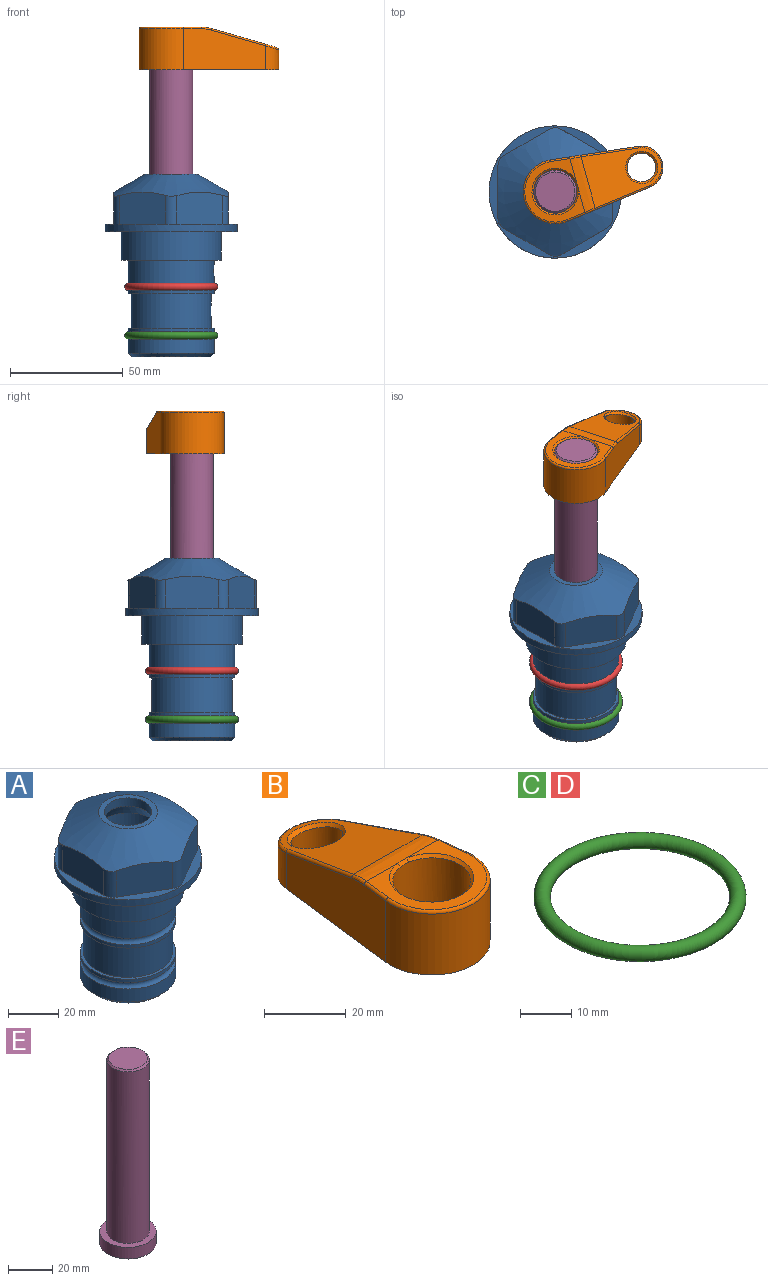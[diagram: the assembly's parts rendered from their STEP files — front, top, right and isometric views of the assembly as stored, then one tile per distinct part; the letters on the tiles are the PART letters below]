
ASSEMBLY  parts=5 mates=4
PART A: 36 faces, bbox 58.7x58.7x81 mm
  f0: cylinder r=17.78mm len=35.56mm, axis (0,0,1), area 1670.8mm2, adj f23,f24,f31
  f1: cylinder r=19.05mm len=38.1mm, axis (0,0,1), area 1191.9mm2, adj f26,f27,f30
  f2: plane 58.66x58.66mm, normal (0,0,-1), area 1150.6mm2, adj f3,f28
  f3: cylinder r=29.33mm len=58.66mm, axis (0,0,-1), area 585.1mm2, adj f2,f4
  f4: plane 58.66x58.66mm, normal (0,0,1), area 475.9mm2, adj f3,f5,f6,f7,f8,f9,f10,f11
  f5: plane 20.32x14.34mm, normal (-0.5,0.87,0), area 324.4mm2, adj f4,f15,f16,f17
  f6: plane 20.32x14.34mm, normal (0.5,0.87,0), area 324.4mm2, adj f4,f14,f15,f17
  f7: plane 23.48x14.34mm, normal (1,0,0), area 324.4mm2, adj f4,f13,f14,f17
  f8: plane 20.32x14.34mm, normal (0.5,-0.87,0), area 324.4mm2, adj f4,f12,f13,f17
  f9: plane 20.32x14.34mm, normal (-0.5,-0.87,0), area 324.4mm2, adj f4,f11,f12,f17
  f10: plane 23.48x14.34mm, normal (-1,0,0), area 324.4mm2, adj f4,f11,f16,f17
  f11: cylinder r=5.08mm len=12.85mm, axis (0,0,-1), area 67.2mm2, adj f4,f9,f10,f17
  f12: cylinder r=5.08mm len=12.85mm, axis (0,0,-1), area 67.2mm2, adj f4,f8,f9,f17
  f13: cylinder r=5.08mm len=12.85mm, axis (0,0,-1), area 67.2mm2, adj f4,f7,f8,f17
  f14: cylinder r=5.08mm len=12.85mm, axis (0,0,-1), area 67.2mm2, adj f4,f6,f7,f17
  f15: cylinder r=5.08mm len=12.85mm, axis (0,0,-1), area 67.2mm2, adj f4,f5,f6,f17
  f16: cylinder r=5.08mm len=12.85mm, axis (0,0,-1), area 67.2mm2, adj f4,f5,f10,f17
  f17: cone r=11.73mm half-angle=60deg, axis (0,0,-1), area 2071.8mm2, adj f5,f6,f7,f8,f9,f10,f11,f12
  f18: plane 23.46x23.46mm, normal (0,0,1), area 147.4mm2, adj f17,f35
  f19: plane 34.93x34.93mm, normal (0,0,-1), area 958mm2, adj f29
  f20: cylinder r=19.05mm len=38.1mm, axis (0,0,1), area 760.1mm2, adj f21,f29
  f21: torus R=19.05mm, axis (0,0,1), area 565.3mm2, adj f20,f22
  f22: cylinder r=19.05mm len=38.1mm, axis (0,0,1), area 190mm2, adj f21,f23
  f23: plane 38.1x38.1mm, normal (0,0,1), area 146.9mm2, adj f0,f22
  f24: plane 38.1x38.1mm, normal (0,0,-1), area 146.9mm2, adj f0,f25
  f25: cylinder r=19.05mm len=38.1mm, axis (0,0,1), area 190mm2, adj f24,f26
  f26: torus R=19.05mm, axis (0,0,1), area 565.3mm2, adj f1,f25
  f27: plane 44.45x44.45mm, normal (0,0,-1), area 411.7mm2, adj f1,f28
  f28: cylinder r=22.23mm len=44.45mm, axis (0,0,1), area 1773.5mm2, adj f2,f27
  f29: cone r=19.05mm half-angle=45deg, axis (0,0,1), area 257.5mm2, adj f19,f20
  f30: cylinder r=3.17mm len=6.75mm, axis (-1,0,0), area 128mm2, adj f1,f33
  f31: cylinder r=3.17mm len=6.35mm, axis (-1,0,0), area 102.5mm2, adj f0,f33
  f32: plane 25.4x25.4mm, normal (0,0,1), area 506.7mm2, adj f33
  f33: cylinder r=12.7mm len=66.42mm, axis (0,0,-1), area 5236.2mm2, adj f30,f31,f32,f34
  f34: cone r=9.53mm half-angle=30deg, axis (0,0,-1), area 443.4mm2, adj f33,f35
  f35: cylinder r=9.53mm len=19.05mm, axis (0,0,-1), area 240.9mm2, adj f18,f34
PART B: 31 faces, bbox 31.7x65.5x19.8 mm
  f0: plane 39.12x18.26mm, normal (0.99,0.12,0), area 612.2mm2, adj f1,f4,f7,f11,f13,f15
  f1: cylinder r=9.53mm len=18.91mm, axis (0,0,-1), area 296.1mm2, adj f0,f2,f7,f17
  f2: plane 39.12x18.26mm, normal (-0.99,0.12,0), area 612.2mm2, adj f1,f4,f7,f12,f14,f16
  f3: cylinder r=6.35mm len=12.7mm, axis (0,0,-1), area 362.4mm2, adj f7,f18
  f4: cylinder r=14.29mm len=28.58mm, axis (0,0,-1), area 882.2mm2, adj f0,f2,f7,f10
  f5: cylinder r=9.53mm len=19.05mm, axis (0,0,-1), area 1092.6mm2, adj f7,f19,f20
  f6: plane 26.99x23.69mm, normal (0,0,1), area 216.2mm2, adj f9,f10,f11,f12,f19
  f7: plane 63.5x28.58mm, normal (0,0,-1), area 661.8mm2, adj f0,f1,f2,f3,f4,f5,f22,f23
  f8: plane 33.52x23.6mm, normal (0,0.26,0.97), area 486mm2, adj f9,f15,f16,f17,f18
  f9: cylinder r=19.05mm len=24.72mm, axis (1,0,0), area 120.4mm2, adj f6,f8,f13,f14,f20
  f10: torus R=13.49mm, axis (0,0,1), area 59mm2, adj f4,f6,f11,f12
  f11: cylinder r=0.79mm len=8.67mm, axis (0.12,-0.99,0), area 10.8mm2, adj f0,f6,f10,f13
  f12: cylinder r=0.79mm len=8.67mm, axis (0.12,0.99,0), area 10.8mm2, adj f2,f6,f10,f14
  f13: bspline ~4.95x1.42mm, area 6.1mm2, adj f0,f9,f11,f15
  f14: bspline ~4.95x1.42mm, area 6.1mm2, adj f2,f9,f12,f16
  f15: cylinder r=0.79mm len=25.95mm, axis (0.12,-0.96,0.26), area 32.9mm2, adj f0,f8,f13,f17
  f16: cylinder r=0.79mm len=25.95mm, axis (0.12,0.96,-0.26), area 32.9mm2, adj f2,f8,f14,f17
  f17: bspline ~18.91x8.38mm, area 30mm2, adj f1,f8,f15,f16
  f18: bspline ~14.29x14.29mm, area 48.3mm2, adj f3,f8
  f19: cone r=9.53mm half-angle=45deg, axis (0,0,1), area 66.5mm2, adj f5,f6,f20
  f20: bspline ~3.22x0.96mm, area 3.5mm2, adj f5,f9,f19
  f21: plane 2.75x2.72mm, normal (0,0,-1), area 2.9mm2, adj f23,f25,f28
  f22: plane 23.05x15.88mm, normal (-0.99,-0.12,0), area 323.6mm2, adj f7,f25,f26,f27,f28,f29
  f23: plane 23.05x15.88mm, normal (0.99,-0.12,0), area 323.6mm2, adj f7,f21,f25,f27,f28,f30
  f24: cylinder r=9.53mm len=10.69mm, axis (0,0,-1), area 114.7mm2, adj f7,f27,f29,f30
  f25: cylinder r=12.7mm len=20.59mm, axis (0,0,-1), area 381.1mm2, adj f7,f21,f22,f23,f26,f28
  f26: plane 2.75x2.72mm, normal (0,0,-1), area 2.9mm2, adj f22,f25,f28
  f27: plane 19.72x18.37mm, normal (0,-0.26,-0.97), area 291.8mm2, adj f22,f23,f24,f28,f29,f30
  f28: cylinder r=15.88mm len=19.92mm, axis (1,0,0), area 54.8mm2, adj f21,f22,f23,f25,f26,f27
  f29: cylinder r=1.59mm len=11mm, axis (0,0,-1), area 34.7mm2, adj f7,f22,f24,f27
  f30: cylinder r=1.59mm len=11mm, axis (0,0,-1), area 34.7mm2, adj f7,f23,f24,f27
PART C: 1 faces, bbox 44.7x44.7x3.2 mm
  f0: torus R=19.05mm, axis (0,0,1), area 1193.9mm2
PART D: same geometry as C
PART E: 6 faces, bbox 25.4x25.4x101.6 mm
  f0: plane 17.46x17.46mm, normal (0,0,1), area 239.5mm2, adj f5
  f1: plane 25.4x25.4mm, normal (0,0,-1), area 506.7mm2, adj f2
  f2: cylinder r=12.7mm len=25.4mm, axis (0,0,1), area 506.7mm2, adj f1,f3
  f3: plane 25.4x25.4mm, normal (0,0,1), area 221.7mm2, adj f2,f4
  f4: cylinder r=9.53mm len=94.46mm, axis (0,0,1), area 5653mm2, adj f3,f5
  f5: cone r=8.73mm half-angle=45deg, axis (0,0,-1), area 64.4mm2, adj f0,f4
PLACE A at identity fixed
PLACE B rot(axis=(0,0,-1),74.3deg) t=(0,0,27.24)mm
PLACE C t=(0,0,-21.59)mm
PLACE D at identity
PLACE E rot(axis=(0,0,-1),74.3deg) t=(0,0,27.24)mm
MATE fastened B.f4 <-> E.f2  axis (0,0,1) through (0,0,90.74)mm
MATE fastened C.f0 <-> A.f0  axis (0,0,1) through (0,0,-46.1)mm
MATE cylindrical A.f0 <-> E.f2  axis (0,0,1) through (0,0,-50.86)mm
MATE fastened A.f0 <-> D.f0  axis (0,0,1) through (0,0,-24.51)mm
